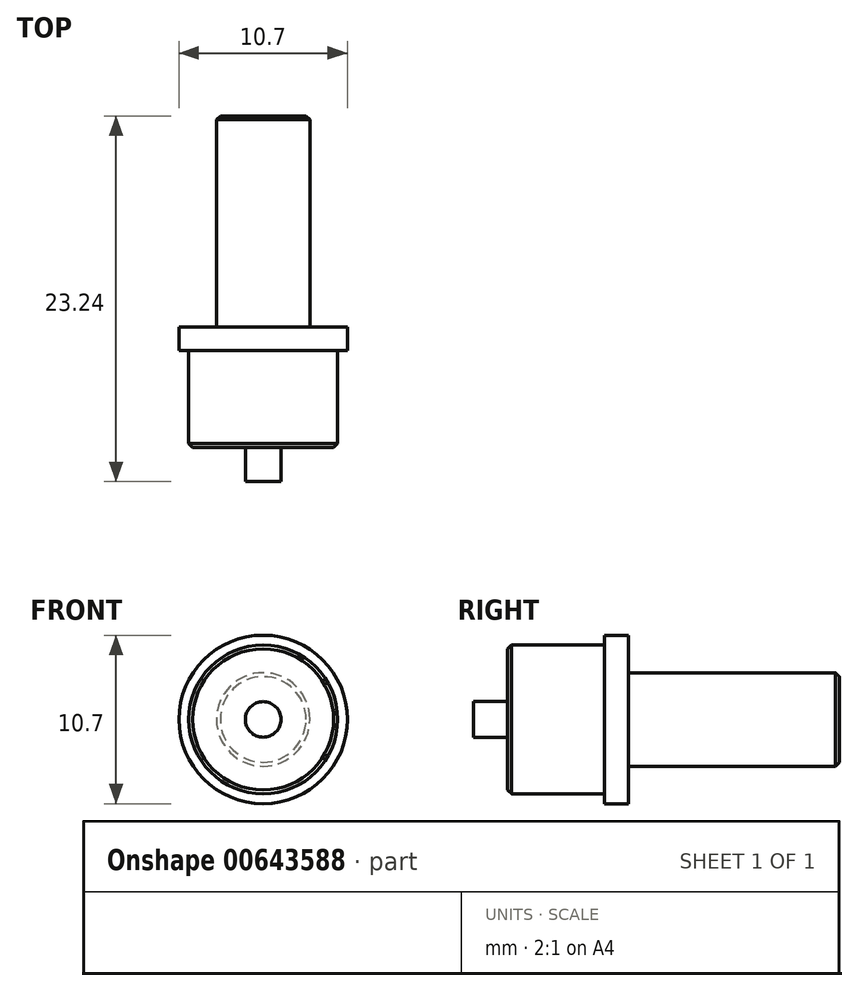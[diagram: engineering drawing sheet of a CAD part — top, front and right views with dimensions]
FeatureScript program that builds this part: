
annotation { "Feature Type Name" : "Feature", "Feature Type Description" : "" }
export const myFeature = defineFeature(function(context is Context, id is Id, definition is map)
    precondition{}
    {
        {
            var Q0;
            Q0=qCreatedBy(makeId("Front.planeOp"),FACE);
            var sketch = newSketch(context, id + "F0", { "sketchPlane" : qUnion([Q0])});
            skCircle(sketch, "E0", {"center": v(0, 0) * mm, "radius": 5.35 * mm});
            skSolve(sketch);
        }
        {
            var Q0;
            Q0=makeQuery(id+"F0.imprint","IMPRINT",FACE,{"disambiguationData":[TD([[makeQuery(id+"F0.imprint","IMPRINT",EDGE,{"derivedFrom":sQuery(id+"F0.wireOp",EDGE,"E0")}),1.0]])]});
            extrude(context, id + "F1", {"entities" : qUnion([Q0]), "depth" : 1.5 * mm, "offsetDistance" : 25 * mm});
        }
        {
            var Q0;
            Q0=makeQuery(id+"F1.opExtrude","CAP_FACE",FACE,{"disambiguationData":[OSD([sQuery(id+"F0.wireOp",EDGE,"E0")])],"isStart":false});
            var sketch = newSketch(context, id + "F2", { "sketchPlane" : qUnion([Q0])});
            skCircle(sketch, "E1", {"center": v(0, 0) * mm, "radius": 4.73 * mm});
            skSolve(sketch);
        }
        {
            var Q0;
            Q0=makeQuery(id+"F2.imprint","IMPRINT",FACE,{"disambiguationData":[TD([[makeQuery(id+"F2.imprint","IMPRINT",EDGE,{"derivedFrom":sQuery(id+"F2.wireOp",EDGE,"E1")}),1.0]])]});
            extrude(context, id + "F3", {"entities" : qUnion([Q0]), "operationType" : NewBodyOperationType.ADD, "depth" : 6.16 * mm, "offsetDistance" : 25 * mm});
        }
        {
            var Q0;
            Q0=makeQuery(id+"F3.opExtrude","CAP_FACE",FACE,{"disambiguationData":[OSD([sQuery(id+"F2.wireOp",EDGE,"E1")])],"isStart":false});
            var sketch = newSketch(context, id + "F4", { "sketchPlane" : qUnion([Q0])});
            skCircle(sketch, "E2", {"center": v(0, 0) * mm, "radius": 1.13 * mm});
            skSolve(sketch);
        }
        {
            var Q0;
            Q0 = qSketchRegion(id + "F4", true);
            extrude(context, id + "F5", {"entities" : qUnion([Q0]), "operationType" : NewBodyOperationType.ADD, "depth" : 2.18 * mm, "offsetDistance" : 25 * mm});
        }
        {
            var Q0;
            Q0=makeQuery(id+"F1.opExtrude","CAP_FACE",FACE,{"disambiguationData":[OSD([sQuery(id+"F0.wireOp",EDGE,"E0")])],"isStart":true});
            var sketch = newSketch(context, id + "F6", { "sketchPlane" : qUnion([Q0])});
            skCircle(sketch, "E3", {"center": v(0, 0) * mm, "radius": 2.97 * mm});
            skSolve(sketch);
        }
        {
            var Q0;
            Q0 = qSketchRegion(id + "F6", true);
            extrude(context, id + "F7", {"entities" : qUnion([Q0]), "operationType" : NewBodyOperationType.ADD, "depth" : 13.4 * mm, "offsetDistance" : 25 * mm});
        }
        {
            var Q0;
            Q0=makeQuery(id+"F3.opExtrude","CAP_EDGE",EDGE,{"disambiguationData":[OSD([sQuery(id+"F2.wireOp",EDGE,"E1")])],"isStart":false});
            var Q1;
            Q1=makeQuery(id+"F7.opExtrude","CAP_EDGE",EDGE,{"disambiguationData":[OSD([sQuery(id+"F6.wireOp",EDGE,"E3")])],"isStart":false});
            chamfer(context, id + "F8", {"entities" : qUnion([Q0, Q1]), "width" : 0.25 * mm, "tangentPropagation" : true});
        }
    });
